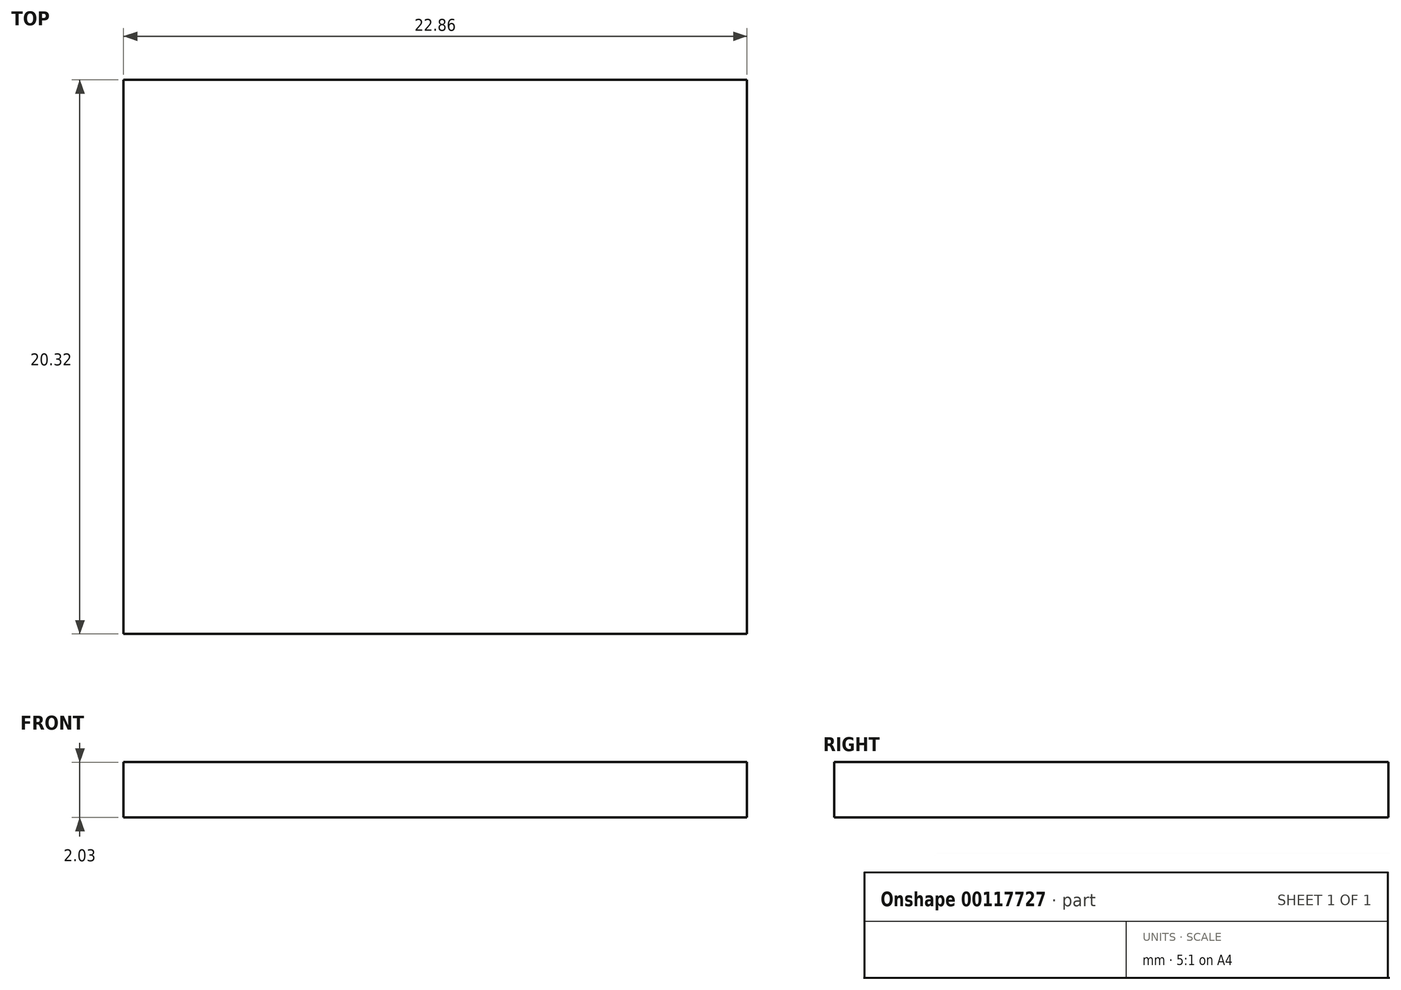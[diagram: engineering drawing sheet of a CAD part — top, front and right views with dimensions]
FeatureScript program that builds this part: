
annotation { "Feature Type Name" : "Feature", "Feature Type Description" : "" }
export const myFeature = defineFeature(function(context is Context, id is Id, definition is map)
    precondition{}
    {
        {
            var Q0;
            Q0=qCreatedBy(makeId("Top.planeOp"),FACE);
            var sketch = newSketch(context, id + "F0", { "sketchPlane" : qUnion([Q0])});
            skLineSegment(sketch, "E0.bottom", {"start": v(11.43, 10.16) * mm, "end": v(-11.43, 10.16) * mm});
            skLineSegment(sketch, "E0.top", {"start": v(11.43, -10.16) * mm, "end": v(-11.43, -10.16) * mm});
            skLineSegment(sketch, "E0.left", {"start": v(11.43, 10.16) * mm, "end": v(11.43, -10.16) * mm});
            skLineSegment(sketch, "E0.right", {"start": v(-11.43, 10.16) * mm, "end": v(-11.43, -10.16) * mm});
            skPoint(sketch, "E0.middle", {"position": v(0, 0) * mm});
            skSolve(sketch);
        }
        {
            var Q0;
            Q0=makeQuery(id+"F0.imprint","IMPRINT",FACE,{"disambiguationData":[TD([[makeQuery(id+"F0.imprint","IMPRINT",EDGE,{"derivedFrom":sQuery(id+"F0.wireOp",EDGE,"E0.bottom")}),1.0]])]});
            extrude(context, id + "F1", {"entities" : qUnion([Q0]), "depth" : 2.03 * mm});
        }
    });
